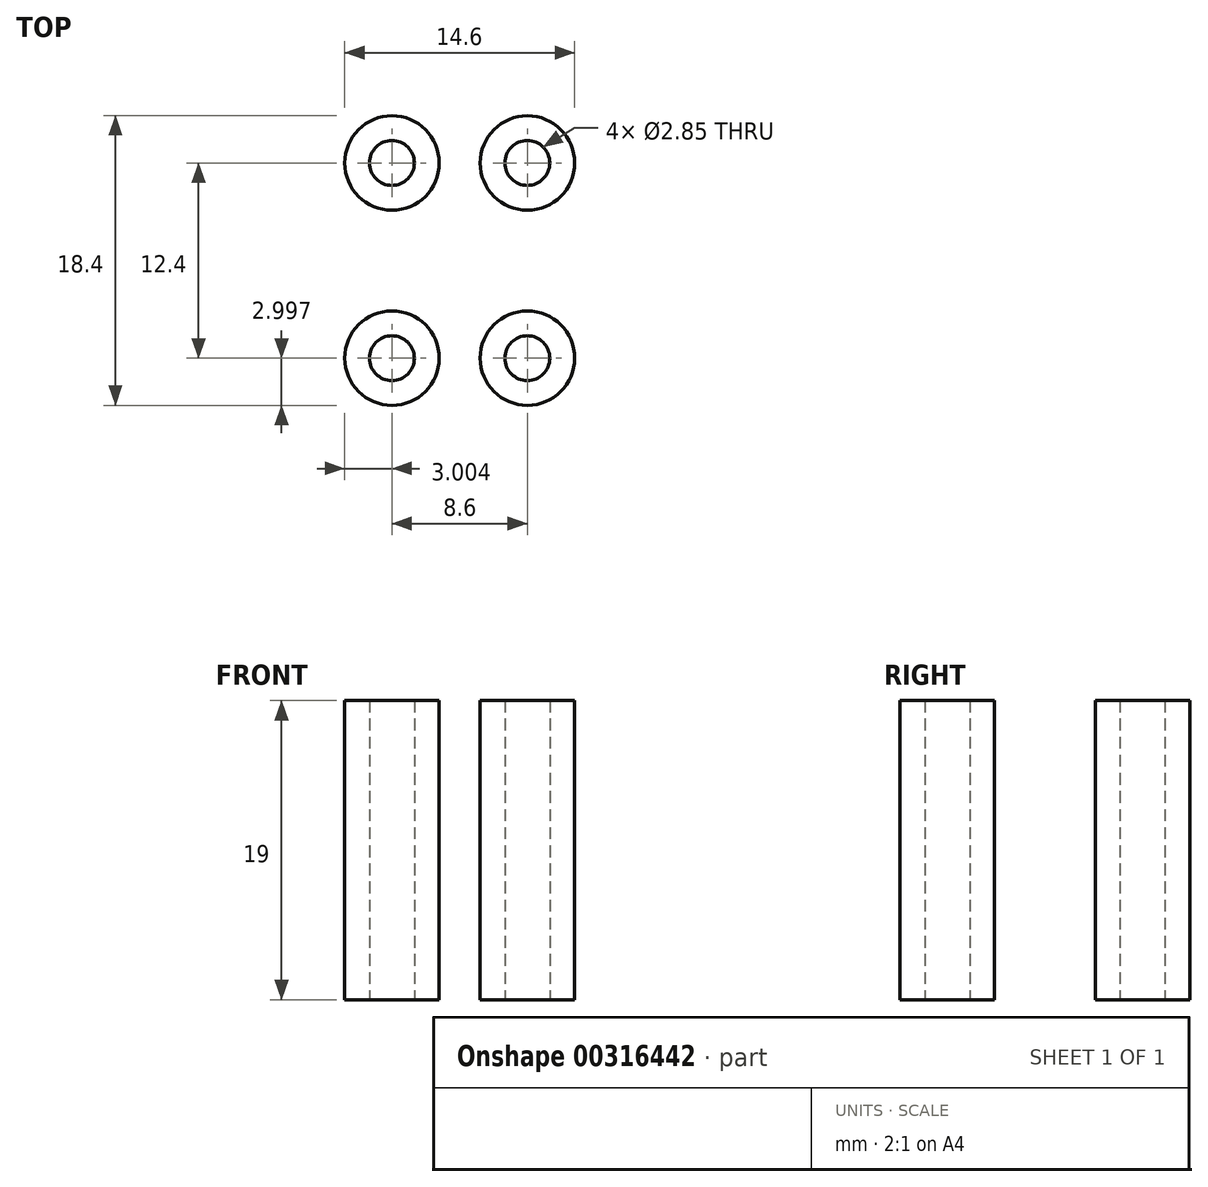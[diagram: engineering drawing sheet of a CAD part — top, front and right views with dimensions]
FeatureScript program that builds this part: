
annotation { "Feature Type Name" : "Feature", "Feature Type Description" : "" }
export const myFeature = defineFeature(function(context is Context, id is Id, definition is map)
    precondition{}
    {
        {
            var Q0;
            Q0=qCreatedBy(makeId("Top.planeOp"),FACE);
            var sketch = newSketch(context, id + "F0", { "sketchPlane" : qUnion([Q0])});
            skCircle(sketch, "E0", {"center": v(-39.26, 27.4) * mm, "radius": 3 * mm});
            skCircle(sketch, "E1", {"center": v(-39.26, 27.4) * mm, "radius": 1.43 * mm});
            skCircle(sketch, "E2.0.1.0", {"center": v(-39.26, 39.8) * mm, "radius": 3 * mm});
            skCircle(sketch, "E2.0.1.1", {"center": v(-39.26, 39.8) * mm, "radius": 1.43 * mm});
            skCircle(sketch, "E2.1.0.0", {"center": v(-30.66, 27.4) * mm, "radius": 3 * mm});
            skCircle(sketch, "E2.1.0.1", {"center": v(-30.66, 27.4) * mm, "radius": 1.43 * mm});
            skCircle(sketch, "E2.1.1.0", {"center": v(-30.66, 39.8) * mm, "radius": 3 * mm});
            skCircle(sketch, "E2.1.1.1", {"center": v(-30.66, 39.8) * mm, "radius": 1.43 * mm});
            skLineSegment(sketch, "E2.direction1", {"start": v(-39.26, 27.4) * mm, "end": v(-30.66, 27.4) * mm, "construction": true});
            skLineSegment(sketch, "E2.direction2", {"start": v(-39.26, 27.4) * mm, "end": v(-39.26, 39.8) * mm, "construction": true});
            skSolve(sketch);
        }
        {
            var Q0;
            Q0=makeQuery(id+"F0.imprint","IMPRINT",FACE,{"disambiguationData":[TD([[makeQuery(id+"F0.imprint","IMPRINT",EDGE,{"derivedFrom":sQuery(id+"F0.wireOp",EDGE,"E2.0.1.0")}),1.0]])]});
            var Q1;
            Q1=makeQuery(id+"F0.imprint","IMPRINT",FACE,{"disambiguationData":[TD([[makeQuery(id+"F0.imprint","IMPRINT",EDGE,{"derivedFrom":sQuery(id+"F0.wireOp",EDGE,"E2.1.1.0")}),1.0]])]});
            var Q2;
            Q2=makeQuery(id+"F0.imprint","IMPRINT",FACE,{"disambiguationData":[TD([[makeQuery(id+"F0.imprint","IMPRINT",EDGE,{"derivedFrom":sQuery(id+"F0.wireOp",EDGE,"E2.1.0.0")}),1.0]])]});
            var Q3;
            Q3=makeQuery(id+"F0.imprint","IMPRINT",FACE,{"disambiguationData":[TD([[makeQuery(id+"F0.imprint","IMPRINT",EDGE,{"derivedFrom":sQuery(id+"F0.wireOp",EDGE,"E0")}),1.0]])]});
            extrude(context, id + "F1", {"entities" : qUnion([Q0, Q1, Q2, Q3]), "depth" : 19 * mm, "offsetDistance" : 25 * mm});
        }
    });
